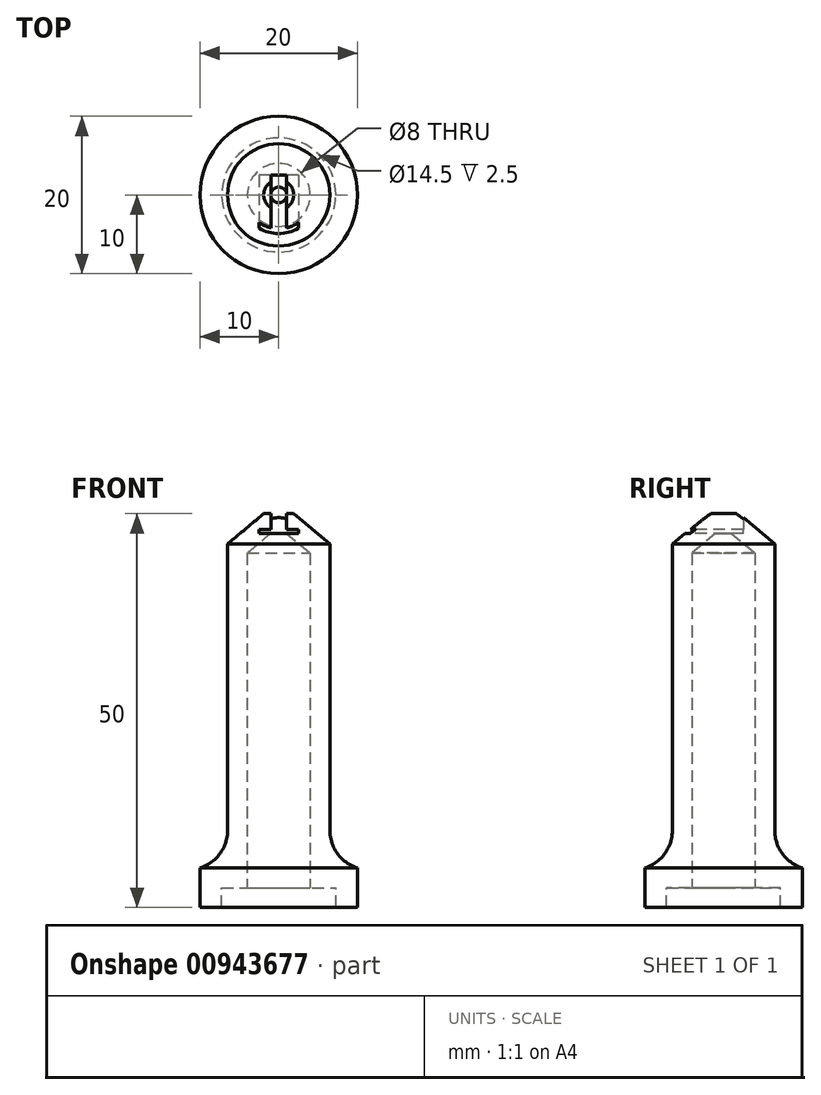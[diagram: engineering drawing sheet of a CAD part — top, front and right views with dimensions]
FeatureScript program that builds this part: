
annotation { "Feature Type Name" : "Feature", "Feature Type Description" : "" }
export const myFeature = defineFeature(function(context is Context, id is Id, definition is map)
    precondition{}
    {
        {
            var Q0;
            Q0=qCreatedBy(makeId("Front.planeOp"),FACE);
            var sketch = newSketch(context, id + "F0", { "sketchPlane" : qUnion([Q0])});
            skLineSegment(sketch, "E0.bottom", {"start": v(0, 0) * mm, "end": v(-4, 0) * mm});
            skLineSegment(sketch, "E0.top", {"start": v(0, 40) * mm, "end": v(-4, 40) * mm});
            skLineSegment(sketch, "E0.left", {"start": v(0, 0) * mm, "end": v(0, 40) * mm});
            skLineSegment(sketch, "E0.right", {"start": v(-4, 0) * mm, "end": v(-4, 40) * mm});
            skLineSegment(sketch, "E1.bottom", {"start": v(0, 40) * mm, "end": v(-1, 40) * mm});
            skLineSegment(sketch, "E1.top", {"start": v(0, 42.5) * mm, "end": v(-1, 42.5) * mm});
            skLineSegment(sketch, "E1.left", {"start": v(0, 40) * mm, "end": v(0, 42.5) * mm});
            skLineSegment(sketch, "E1.right", {"start": v(-1, 40) * mm, "end": v(-1, 42.5) * mm});
            skLineSegment(sketch, "E2", {"start": v(-4, 40) * mm, "end": v(-1, 42.5) * mm});
            skLineSegment(sketch, "E3.0", {"start": v(0, 45) * mm, "end": v(-1.9, 45) * mm});
            skLineSegment(sketch, "E3.1", {"start": v(-6.5, 41.17) * mm, "end": v(-1.9, 45) * mm});
            skLineSegment(sketch, "E3.2", {"start": v(-6.5, 0) * mm, "end": v(-6.5, 41.17) * mm});
            skLineSegment(sketch, "E4", {"start": v(-6.5, 0) * mm, "end": v(-4, 0) * mm});
            skLineSegment(sketch, "E5", {"start": v(0, 45) * mm, "end": v(0, 42.5) * mm});
            skLineSegment(sketch, "E6.bottom", {"start": v(0, 0) * mm, "end": v(-10, 0) * mm});
            skLineSegment(sketch, "E6.top", {"start": v(0, -2.5) * mm, "end": v(-10, -2.5) * mm});
            skLineSegment(sketch, "E6.left", {"start": v(0, 0) * mm, "end": v(0, -2.5) * mm});
            skLineSegment(sketch, "E6.right", {"start": v(-10, 0) * mm, "end": v(-10, -2.5) * mm});
            skLineSegment(sketch, "E7.bottom", {"start": v(-4, 0) * mm, "end": v(-6.5, 0) * mm});
            skLineSegment(sketch, "E7.top", {"start": v(-4, -2.5) * mm, "end": v(-6.5, -2.5) * mm});
            skLineSegment(sketch, "E7.left", {"start": v(-4, 0) * mm, "end": v(-4, -2.5) * mm});
            skLineSegment(sketch, "E7.right", {"start": v(-6.5, 0) * mm, "end": v(-6.5, -2.5) * mm});
            skSolve(sketch);
        }
        {
            var Q0;
            Q0=makeQuery(id+"F0.imprint","IMPRINT",FACE,{"disambiguationData":[TD([[makeQuery(id+"F0.imprint","IMPRINT",EDGE,{"derivedFrom":sQuery(id+"F0.wireOp",EDGE,"E0.right")}),1.0]])]});
            var Q1;
            Q1=makeQuery(id+"F0.imprint","IMPRINT",FACE,{"disambiguationData":[TD([[makeQuery(id+"F0.imprint","IMPRINT",EDGE,{"derivedFrom":sQuery(id+"F0.wireOp",EDGE,"E4")}),-1.0]])]});
            var Q2;
            Q2=makeQuery(id+"F0.imprint","IMPRINT",FACE,{"disambiguationData":[TD([[makeQuery(id+"F0.imprint","IMPRINT",EDGE,{"derivedFrom":sQuery(id+"F0.wireOp",EDGE,"E6.bottom")}),1.0]])]});
            var Q3;
            Q3=sQuery(id+"F0.wireOp",EDGE,"E0.left");
            revolve(context, id + "F1", {"surfaceOperationType" : NewSurfaceOperationType.NEW, "entities" : qUnion([Q0, Q1, Q2]), "axis" : qUnion([Q3]), "revolveType" : RevolveType.FULL});
        }
        {
            var Q0;
            Q0=qCreatedBy(makeId("Front.planeOp"),FACE);
            cPlane(context, id + "F2", {"entities" : qUnion([Q0]), "cplaneType" : CPlaneType.OFFSET, "offset" : 25 * mm, "width" : 150 * mm, "height" : 150 * mm});
        }
        {
            var Q0;
            Q0=qCreatedBy(id+"F2.planeOp",FACE);
            var sketch = newSketch(context, id + "F3", { "sketchPlane" : qUnion([Q0])});
            skLineSegment(sketch, "E8.bottom", {"start": v(2.5, 42.5) * mm, "end": v(-2.5, 42.5) * mm});
            skLineSegment(sketch, "E8.top", {"start": v(2.5, 43) * mm, "end": v(-2.5, 43) * mm});
            skLineSegment(sketch, "E8.left", {"start": v(2.5, 42.5) * mm, "end": v(2.5, 43) * mm});
            skLineSegment(sketch, "E8.right", {"start": v(-2.5, 42.5) * mm, "end": v(-2.5, 43) * mm});
            skPoint(sketch, "E8.middle", {"position": v(0, 42.75) * mm});
            skLineSegment(sketch, "E9.bottom", {"start": v(-1, 45) * mm, "end": v(1, 45) * mm});
            skLineSegment(sketch, "E9.top", {"start": v(-1, 40.5) * mm, "end": v(1, 40.5) * mm});
            skLineSegment(sketch, "E9.left", {"start": v(-1, 45) * mm, "end": v(-1, 40.5) * mm});
            skLineSegment(sketch, "E9.right", {"start": v(1, 45) * mm, "end": v(1, 40.5) * mm});
            skSolve(sketch);
        }
        {
            var Q0;
            {var subQ5=sQuery(id+"F3.wireOp",EDGE,"E9.bottom");Q0=makeQuery(id+"F3.imprint","IMPRINT",FACE,{"disambiguationData":[TD([[makeQuery(id+"F3.imprint","IMPRINT",EDGE,{"derivedFrom":subQ5}),-1.0]])]});}
            var Q1;
            {var subQ0=sQuery(id+"F3.wireOp",EDGE,"E9.right");var subQ1=sQuery(id+"F3.wireOp",EDGE,"E8.bottom");var subQ2=makeQuery(id+"F3.imprint","INTERSECT",VERTEX,{"derivedFrom":[subQ1,subQ0]});Q1=makeQuery(id+"F3.imprint","IMPRINT",FACE,{"disambiguationData":[TD([[makeQuery(id+"F3.imprint","IMPRINT",EDGE,{"disambiguationData":[TD([[subQ2,-1.0]])],"derivedFrom":subQ1}),-1.0]])]});}
            var Q2;
            {var subQ0=sQuery(id+"F3.wireOp",EDGE,"E8.right");Q2=makeQuery(id+"F3.imprint","IMPRINT",FACE,{"disambiguationData":[TD([[makeQuery(id+"F3.imprint","IMPRINT",EDGE,{"derivedFrom":subQ0}),-1.0]])]});}
            var Q3;
            {var subQ3=sQuery(id+"F3.wireOp",EDGE,"E8.left");Q3=makeQuery(id+"F3.imprint","IMPRINT",FACE,{"disambiguationData":[TD([[makeQuery(id+"F3.imprint","IMPRINT",EDGE,{"derivedFrom":subQ3}),1.0]])]});}
            extrude(context, id + "F4", {"entities" : qUnion([Q0, Q1, Q2, Q3]), "operationType" : NewBodyOperationType.REMOVE, "oppositeDirection" : true, "depth" : 27.5 * mm, "offsetDistance" : 25 * mm});
        }
        {
            var Q0;
            Q0=makeQuery(id+"F1.opRevolve","SWEPT_FACE",FACE,{"disambiguationData":[OSD([sQuery(id+"F0.wireOp",EDGE,"E6.top")])]});
            var sketch = newSketch(context, id + "F5", { "sketchPlane" : qUnion([Q0])});
            skCircle(sketch, "E10", {"center": v(0, 0) * mm, "radius": 10 * mm});
            skCircle(sketch, "E11", {"center": v(0, 0) * mm, "radius": 7.25 * mm});
            skSolve(sketch);
        }
        {
            var Q0;
            Q0=makeQuery(id+"F5.imprint","IMPRINT",FACE,{"disambiguationData":[TD([[makeQuery(id+"F5.imprint","IMPRINT",EDGE,{"derivedFrom":sQuery(id+"F5.wireOp",EDGE,"E10")}),1.0]])]});
            extrude(context, id + "F6", {"entities" : qUnion([Q0]), "operationType" : NewBodyOperationType.ADD, "depth" : 2.5 * mm, "offsetDistance" : 25 * mm});
        }
        {
            var Q0;
            Q0=makeQuery(id+"F1.opRevolve","SWEPT_EDGE",EDGE,{"disambiguationData":[OSD([sQuery(id+"F0.wireOp",EDGE,"E3.2"),sQuery(id+"F0.wireOp",EDGE,"E4"),sQuery(id+"F0.wireOp",EDGE,"E6.bottom"),sQuery(id+"F0.wireOp",EDGE,"E7.right")])]});
            fillet(context, id + "F7", {"entities" : qUnion([Q0]), "tangentPropagation" : true, "radius" : 5 * mm, "defaultsChanged" : false, "vertexSettings" : [], "allowEdgeOverflow" : false});
        }
    });
